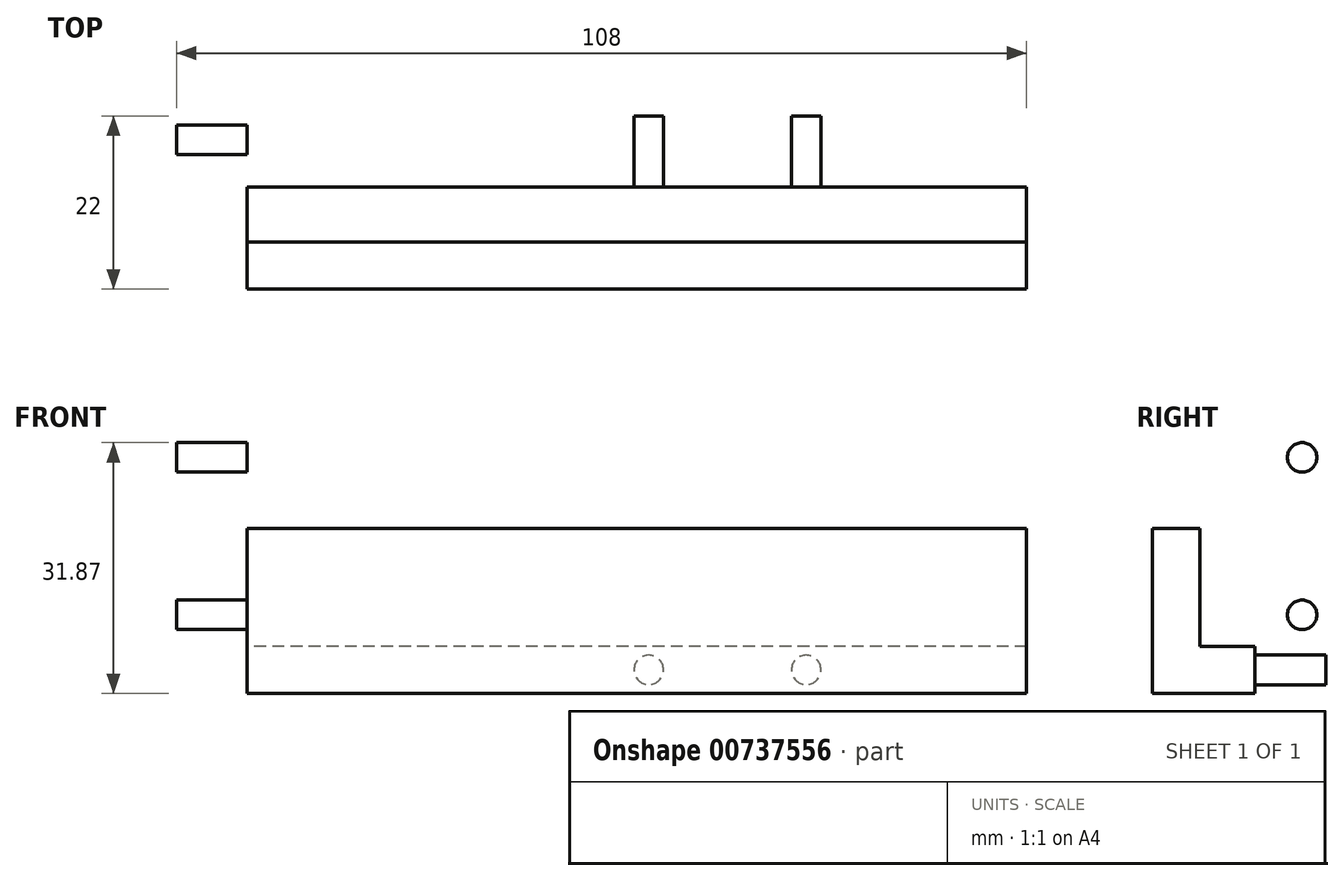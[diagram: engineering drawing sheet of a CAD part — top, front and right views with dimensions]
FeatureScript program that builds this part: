
annotation { "Feature Type Name" : "Feature", "Feature Type Description" : "" }
export const myFeature = defineFeature(function(context is Context, id is Id, definition is map)
    precondition{}
    {
        {
            var Q0;
            Q0=qCreatedBy(makeId("Right.planeOp"),FACE);
            var sketch = newSketch(context, id + "F0", { "sketchPlane" : qUnion([Q0])});
            skLineSegment(sketch, "E0", {"start": v(21.48, 53.88) * mm, "end": v(21.48, -37.12) * mm});
            skLineSegment(sketch, "E1", {"start": v(-0.52, -37.12) * mm, "end": v(21.48, -37.12) * mm});
            skLineSegment(sketch, "E2", {"start": v(-0.52, -37.12) * mm, "end": v(-0.52, -16.12) * mm});
            skLineSegment(sketch, "E3", {"start": v(5.48, -16.12) * mm, "end": v(5.48, -31.12) * mm});
            skLineSegment(sketch, "E4", {"start": v(5.48, -31.12) * mm, "end": v(15.48, -31.12) * mm});
            skLineSegment(sketch, "E5", {"start": v(15.48, -31.12) * mm, "end": v(15.48, 53.88) * mm});
            skLineSegment(sketch, "E6", {"start": v(15.48, 53.88) * mm, "end": v(21.48, 53.88) * mm});
            skLineSegment(sketch, "E7", {"start": v(-0.52, -16.12) * mm, "end": v(5.48, -16.12) * mm});
            skSolve(sketch);
        }
        {
            var Q0;
            Q0=makeQuery(id+"F0.imprint","IMPRINT",FACE,{"disambiguationData":[TD([[makeQuery(id+"F0.imprint","IMPRINT",EDGE,{"derivedFrom":sQuery(id+"F0.wireOp",EDGE,"E0")}),-1.0]])]});
            extrude(context, id + "F1", {"entities" : qUnion([Q0]), "depth" : 100 * mm, "offsetDistance" : 25 * mm});
        }
        {
            var Q0;
            Q0=makeQuery(id+"F1.opExtrude","CAP_FACE",FACE,{"disambiguationData":[OSD([sQuery(id+"F0.wireOp",EDGE,"E0"),sQuery(id+"F0.wireOp",EDGE,"E1"),sQuery(id+"F0.wireOp",EDGE,"E2"),sQuery(id+"F0.wireOp",EDGE,"E3"),sQuery(id+"F0.wireOp",EDGE,"E4"),sQuery(id+"F0.wireOp",EDGE,"E5"),sQuery(id+"F0.wireOp",EDGE,"E6"),sQuery(id+"F0.wireOp",EDGE,"E7")])],"isStart":false});
            var sketch = newSketch(context, id + "F2", { "sketchPlane" : qUnion([Q0])});
            skCircle(sketch, "E8", {"center": v(18.48, 43.88) * mm, "radius": 1.5 * mm});
            skCircle(sketch, "E9", {"center": v(18.48, 23.88) * mm, "radius": 1.5 * mm});
            skCircle(sketch, "E10.MirrorC", {"center": v(18.48, -27.12) * mm, "radius": 1.5 * mm});
            skCircle(sketch, "E11.MirrorC", {"center": v(18.48, -7.12) * mm, "radius": 1.5 * mm});
            skSolve(sketch);
        }
        {
            var Q0;
            Q0=makeQuery(id+"F2.imprint","IMPRINT",FACE,{"disambiguationData":[TD([[makeQuery(id+"F2.imprint","IMPRINT",EDGE,{"derivedFrom":sQuery(id+"F2.wireOp",EDGE,"E8")}),1.0]])]});
            var Q1;
            Q1=makeQuery(id+"F2.imprint","IMPRINT",FACE,{"disambiguationData":[TD([[makeQuery(id+"F2.imprint","IMPRINT",EDGE,{"derivedFrom":sQuery(id+"F2.wireOp",EDGE,"E9")}),1.0]])]});
            var Q2;
            Q2=makeQuery(id+"F2.imprint","IMPRINT",FACE,{"disambiguationData":[TD([[makeQuery(id+"F2.imprint","IMPRINT",EDGE,{"derivedFrom":sQuery(id+"F2.wireOp",EDGE,"E11.MirrorC")}),-1.0]])]});
            var Q3;
            Q3=makeQuery(id+"F2.imprint","IMPRINT",FACE,{"disambiguationData":[TD([[makeQuery(id+"F2.imprint","IMPRINT",EDGE,{"derivedFrom":sQuery(id+"F2.wireOp",EDGE,"E10.MirrorC")}),-1.0]])]});
            extrude(context, id + "F3", {"entities" : qUnion([Q0, Q1, Q2, Q3]), "operationType" : NewBodyOperationType.ADD, "depth" : 8 * mm, "offsetDistance" : 25 * mm});
        }
        {
            var Q0;
            Q0=makeQuery(id+"F1.opExtrude","CAP_FACE",FACE,{"disambiguationData":[OSD([sQuery(id+"F0.wireOp",EDGE,"E0"),sQuery(id+"F0.wireOp",EDGE,"E1"),sQuery(id+"F0.wireOp",EDGE,"E2"),sQuery(id+"F0.wireOp",EDGE,"E3"),sQuery(id+"F0.wireOp",EDGE,"E4"),sQuery(id+"F0.wireOp",EDGE,"E5"),sQuery(id+"F0.wireOp",EDGE,"E6"),sQuery(id+"F0.wireOp",EDGE,"E7")])],"isStart":true});
            var sketch = newSketch(context, id + "F4", { "sketchPlane" : qUnion([Q0])});
            skCircle(sketch, "E12", {"center": v(-18.48, 43.88) * mm, "radius": 1.88 * mm});
            skCircle(sketch, "E13", {"center": v(-18.48, 23.88) * mm, "radius": 1.88 * mm});
            skCircle(sketch, "E14.MirrorC", {"center": v(-18.48, -27.12) * mm, "radius": 1.88 * mm});
            skCircle(sketch, "E15.MirrorC", {"center": v(-18.48, -7.12) * mm, "radius": 1.88 * mm});
            skSolve(sketch);
        }
        {
            var Q0;
            Q0=makeQuery(id+"F4.imprint","IMPRINT",FACE,{"disambiguationData":[TD([[makeQuery(id+"F4.imprint","IMPRINT",EDGE,{"derivedFrom":sQuery(id+"F4.wireOp",EDGE,"E13")}),1.0]])]});
            var Q1;
            Q1=makeQuery(id+"F4.imprint","IMPRINT",FACE,{"disambiguationData":[TD([[makeQuery(id+"F4.imprint","IMPRINT",EDGE,{"derivedFrom":sQuery(id+"F4.wireOp",EDGE,"E12")}),1.0]])]});
            var Q2;
            Q2=makeQuery(id+"F4.imprint","IMPRINT",FACE,{"disambiguationData":[TD([[makeQuery(id+"F4.imprint","IMPRINT",EDGE,{"derivedFrom":sQuery(id+"F4.wireOp",EDGE,"E15.MirrorC")}),-1.0]])]});
            var Q3;
            Q3=makeQuery(id+"F4.imprint","IMPRINT",FACE,{"disambiguationData":[TD([[makeQuery(id+"F4.imprint","IMPRINT",EDGE,{"derivedFrom":sQuery(id+"F4.wireOp",EDGE,"E14.MirrorC")}),-1.0]])]});
            extrude(context, id + "F5", {"entities" : qUnion([Q0, Q1, Q2, Q3]), "operationType" : NewBodyOperationType.REMOVE, "oppositeDirection" : true, "depth" : 9 * mm, "offsetDistance" : 25 * mm});
        }
        {
            var Q0;
            Q0=makeQuery(id+"F1.opExtrude","SWEPT_FACE",FACE,{"disambiguationData":[OSD([sQuery(id+"F0.wireOp",EDGE,"E0")])]});
            var sketch = newSketch(context, id + "F6", { "sketchPlane" : qUnion([Q0])});
            skLineSegment(sketch, "E16", {"start": v(0, -37.12) * mm, "end": v(0, -34.12) * mm});
            skCircle(sketch, "E17", {"center": v(-20, -34.12) * mm, "radius": 1.88 * mm});
            skCircle(sketch, "E18", {"center": v(-40, -34.12) * mm, "radius": 1.88 * mm});
            skCircle(sketch, "E19.MirrorC", {"center": v(-80, -34.12) * mm, "radius": 1.88 * mm});
            skCircle(sketch, "E20.MirrorC", {"center": v(-60, -34.12) * mm, "radius": 1.88 * mm});
            skSolve(sketch);
        }
        {
            var Q0;
            Q0=makeQuery(id+"F6.imprint","IMPRINT",FACE,{"disambiguationData":[TD([[makeQuery(id+"F6.imprint","IMPRINT",EDGE,{"derivedFrom":sQuery(id+"F6.wireOp",EDGE,"E19.MirrorC")}),-1.0]])]});
            var Q1;
            Q1=makeQuery(id+"F6.imprint","IMPRINT",FACE,{"disambiguationData":[TD([[makeQuery(id+"F6.imprint","IMPRINT",EDGE,{"derivedFrom":sQuery(id+"F6.wireOp",EDGE,"E20.MirrorC")}),-1.0]])]});
            var Q2;
            Q2=makeQuery(id+"F6.imprint","IMPRINT",FACE,{"disambiguationData":[TD([[makeQuery(id+"F6.imprint","IMPRINT",EDGE,{"derivedFrom":sQuery(id+"F6.wireOp",EDGE,"E18")}),1.0]])]});
            var Q3;
            Q3=makeQuery(id+"F6.imprint","IMPRINT",FACE,{"disambiguationData":[TD([[makeQuery(id+"F6.imprint","IMPRINT",EDGE,{"derivedFrom":sQuery(id+"F6.wireOp",EDGE,"E17")}),1.0]])]});
            extrude(context, id + "F7", {"entities" : qUnion([Q0, Q1, Q2, Q3]), "operationType" : NewBodyOperationType.REMOVE, "oppositeDirection" : true, "depth" : 9 * mm, "offsetDistance" : 25 * mm});
        }
    });
